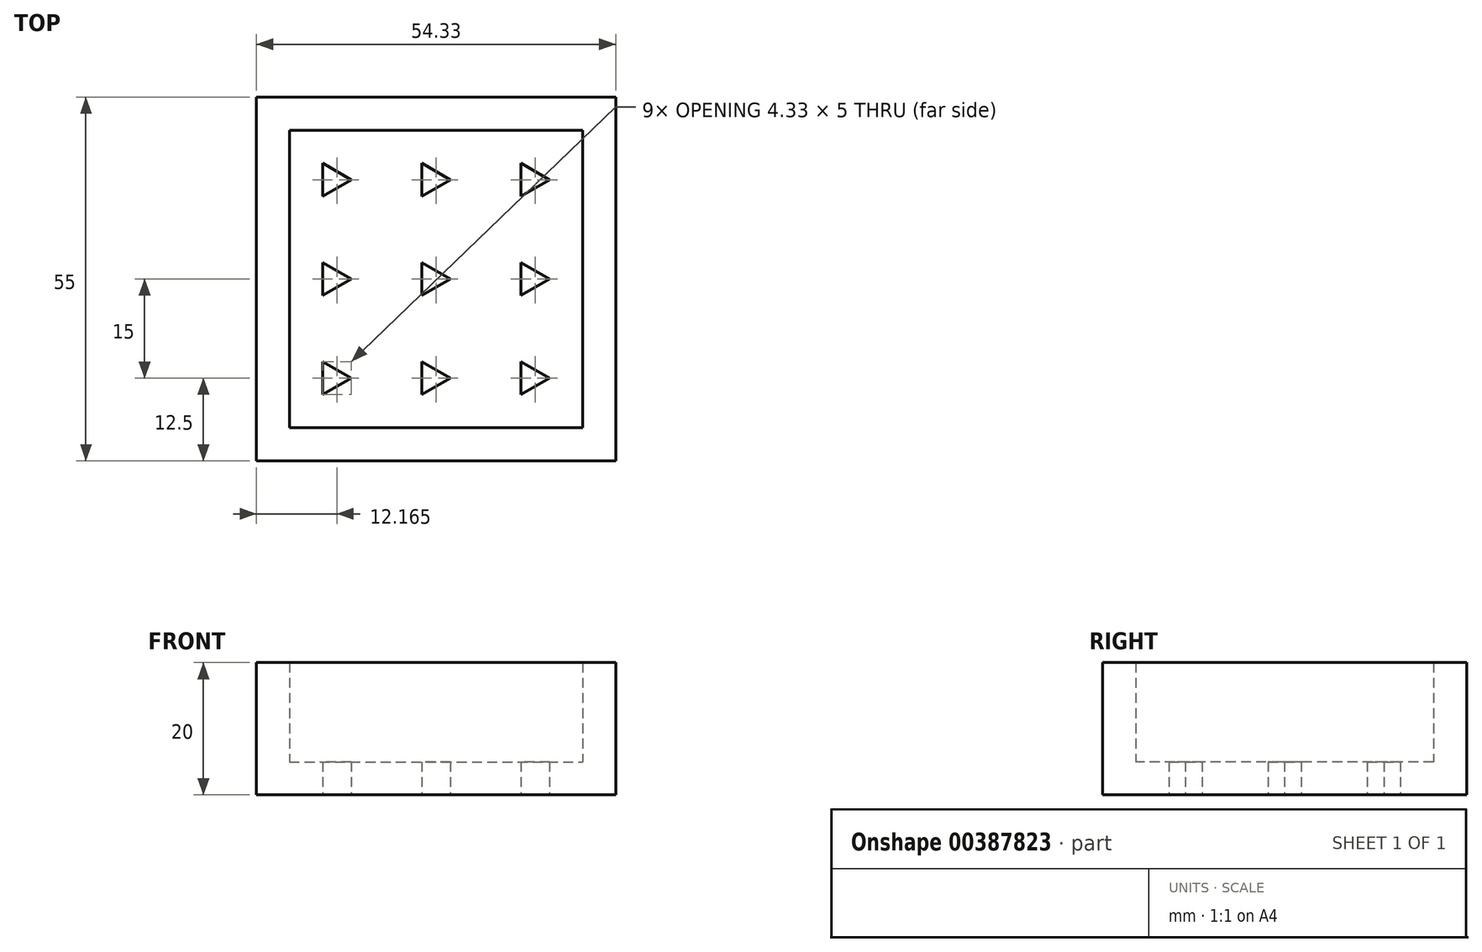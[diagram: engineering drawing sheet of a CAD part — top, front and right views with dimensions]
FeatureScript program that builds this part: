
annotation { "Feature Type Name" : "Feature", "Feature Type Description" : "" }
export const myFeature = defineFeature(function(context is Context, id is Id, definition is map)
    precondition{}
    {
        {
            var Q0;
            Q0=qCreatedBy(makeId("Top.planeOp"),FACE);
            var sketch = newSketch(context, id + "F0", { "sketchPlane" : qUnion([Q0])});
            skLineSegment(sketch, "E0", {"start": v(0, 5) * mm, "end": v(0, 0) * mm});
            skLineSegment(sketch, "E1", {"start": v(0, 0) * mm, "end": v(4.33, 2.5) * mm});
            skLineSegment(sketch, "E2", {"start": v(4.33, 2.5) * mm, "end": v(0, 5) * mm});
            skLineSegment(sketch, "E3.0.1.0", {"start": v(4.33, 17.5) * mm, "end": v(0, 20) * mm});
            skLineSegment(sketch, "E3.0.1.1", {"start": v(0, 15) * mm, "end": v(4.33, 17.5) * mm});
            skLineSegment(sketch, "E3.0.1.2", {"start": v(0, 20) * mm, "end": v(0, 15) * mm});
            skLineSegment(sketch, "E3.0.2.0", {"start": v(4.33, 32.5) * mm, "end": v(0, 35) * mm});
            skLineSegment(sketch, "E3.0.2.1", {"start": v(0, 30) * mm, "end": v(4.33, 32.5) * mm});
            skLineSegment(sketch, "E3.0.2.2", {"start": v(0, 35) * mm, "end": v(0, 30) * mm});
            skLineSegment(sketch, "E3.1.0.0", {"start": v(19.33, 2.5) * mm, "end": v(15, 5) * mm});
            skLineSegment(sketch, "E3.1.0.1", {"start": v(15, 0) * mm, "end": v(19.33, 2.5) * mm});
            skLineSegment(sketch, "E3.1.0.2", {"start": v(15, 5) * mm, "end": v(15, 0) * mm});
            skLineSegment(sketch, "E3.1.1.0", {"start": v(19.33, 17.5) * mm, "end": v(15, 20) * mm});
            skLineSegment(sketch, "E3.1.1.1", {"start": v(15, 15) * mm, "end": v(19.33, 17.5) * mm});
            skLineSegment(sketch, "E3.1.1.2", {"start": v(15, 20) * mm, "end": v(15, 15) * mm});
            skLineSegment(sketch, "E3.1.2.0", {"start": v(19.33, 32.5) * mm, "end": v(15, 35) * mm});
            skLineSegment(sketch, "E3.1.2.1", {"start": v(15, 30) * mm, "end": v(19.33, 32.5) * mm});
            skLineSegment(sketch, "E3.1.2.2", {"start": v(15, 35) * mm, "end": v(15, 30) * mm});
            skLineSegment(sketch, "E3.2.0.0", {"start": v(34.33, 2.5) * mm, "end": v(30, 5) * mm});
            skLineSegment(sketch, "E3.2.0.1", {"start": v(30, 0) * mm, "end": v(34.33, 2.5) * mm});
            skLineSegment(sketch, "E3.2.0.2", {"start": v(30, 5) * mm, "end": v(30, 0) * mm});
            skLineSegment(sketch, "E3.2.1.0", {"start": v(34.33, 17.5) * mm, "end": v(30, 20) * mm});
            skLineSegment(sketch, "E3.2.1.1", {"start": v(30, 15) * mm, "end": v(34.33, 17.5) * mm});
            skLineSegment(sketch, "E3.2.1.2", {"start": v(30, 20) * mm, "end": v(30, 15) * mm});
            skLineSegment(sketch, "E3.2.2.0", {"start": v(34.33, 32.5) * mm, "end": v(30, 35) * mm});
            skLineSegment(sketch, "E3.2.2.1", {"start": v(30, 30) * mm, "end": v(34.33, 32.5) * mm});
            skLineSegment(sketch, "E3.2.2.2", {"start": v(30, 35) * mm, "end": v(30, 30) * mm});
            skLineSegment(sketch, "E3.direction1", {"start": v(0, 0) * mm, "end": v(15, 0) * mm, "construction": true});
            skLineSegment(sketch, "E3.direction2", {"start": v(0, 0) * mm, "end": v(0, 15) * mm, "construction": true});
            skLineSegment(sketch, "E4.bottom", {"start": v(-10, 45) * mm, "end": v(44.33, 45) * mm});
            skLineSegment(sketch, "E4.top", {"start": v(-10, -10) * mm, "end": v(44.33, -10) * mm});
            skLineSegment(sketch, "E4.left", {"start": v(-10, 45) * mm, "end": v(-10, -10) * mm});
            skLineSegment(sketch, "E4.right", {"start": v(44.33, 45) * mm, "end": v(44.33, -10) * mm});
            skSolve(sketch);
        }
        {
            var Q0;
            Q0 = qSketchRegion(id + "F0", true);
            extrude(context, id + "F1", {"entities" : qUnion([Q0]), "depth" : 5 * mm});
        }
        {
            var Q0;
            Q0=makeQuery(id+"F1.opExtrude","CAP_FACE",FACE,{"disambiguationData":[OSD([sQuery(id+"F0.wireOp",EDGE,"E0"),sQuery(id+"F0.wireOp",EDGE,"E1"),sQuery(id+"F0.wireOp",EDGE,"E2"),sQuery(id+"F0.wireOp",EDGE,"E3.0.1.0"),sQuery(id+"F0.wireOp",EDGE,"E3.0.1.1"),sQuery(id+"F0.wireOp",EDGE,"E3.0.1.2"),sQuery(id+"F0.wireOp",EDGE,"E3.0.2.0"),sQuery(id+"F0.wireOp",EDGE,"E3.0.2.1"),sQuery(id+"F0.wireOp",EDGE,"E3.0.2.2"),sQuery(id+"F0.wireOp",EDGE,"E3.1.0.0"),sQuery(id+"F0.wireOp",EDGE,"E3.1.0.1"),sQuery(id+"F0.wireOp",EDGE,"E3.1.0.2"),sQuery(id+"F0.wireOp",EDGE,"E3.1.1.0"),sQuery(id+"F0.wireOp",EDGE,"E3.1.1.1"),sQuery(id+"F0.wireOp",EDGE,"E3.1.1.2"),sQuery(id+"F0.wireOp",EDGE,"E3.1.2.0"),sQuery(id+"F0.wireOp",EDGE,"E3.1.2.1"),sQuery(id+"F0.wireOp",EDGE,"E3.1.2.2"),sQuery(id+"F0.wireOp",EDGE,"E3.2.0.0"),sQuery(id+"F0.wireOp",EDGE,"E3.2.0.1"),sQuery(id+"F0.wireOp",EDGE,"E3.2.0.2"),sQuery(id+"F0.wireOp",EDGE,"E3.2.1.0"),sQuery(id+"F0.wireOp",EDGE,"E3.2.1.1"),sQuery(id+"F0.wireOp",EDGE,"E3.2.1.2"),sQuery(id+"F0.wireOp",EDGE,"E3.2.2.0"),sQuery(id+"F0.wireOp",EDGE,"E3.2.2.1"),sQuery(id+"F0.wireOp",EDGE,"E3.2.2.2"),sQuery(id+"F0.wireOp",EDGE,"E4.bottom"),sQuery(id+"F0.wireOp",EDGE,"E4.top"),sQuery(id+"F0.wireOp",EDGE,"E4.left"),sQuery(id+"F0.wireOp",EDGE,"E4.right")])],"isStart":false});
            var sketch = newSketch(context, id + "F2", { "sketchPlane" : qUnion([Q0])});
            skLineSegment(sketch, "E5.0", {"start": v(-5, 40) * mm, "end": v(-5, -5) * mm});
            skLineSegment(sketch, "E5.1", {"start": v(39.33, 40) * mm, "end": v(-5, 40) * mm});
            skLineSegment(sketch, "E5.2", {"start": v(39.33, -5) * mm, "end": v(39.33, 40) * mm});
            skLineSegment(sketch, "E5.3", {"start": v(-5, -5) * mm, "end": v(39.33, -5) * mm});
            skSolve(sketch);
        }
        {
            var Q0;
            Q0=makeQuery(id+"F2.imprint","IMPRINT",FACE,{"disambiguationData":[TD([[makeQuery(id+"F2.imprint","IMPRINT",EDGE,{"derivedFrom":sQuery(id+"F2.wireOp",EDGE,"E5.0")}),-1.0]])]});
            var sketch = newSketch(context, id + "F3", { "sketchPlane" : qUnion([Q0])});
            skSolve(sketch);
        }
        {
            var Q0;
            Q0 = qSketchRegion(id + "F3", true);
            var Q1;
            Q1=makeQuery(id+"F2.imprint","IMPRINT",FACE,{"disambiguationData":[TD([[makeQuery(id+"F2.imprint","IMPRINT",EDGE,{"derivedFrom":sQuery(id+"F2.wireOp",EDGE,"E5.0")}),-1.0]])]});
            extrude(context, id + "F4", {"entities" : qUnion([Q0, Q1]), "operationType" : NewBodyOperationType.ADD, "depth" : 15 * mm});
        }
    });
